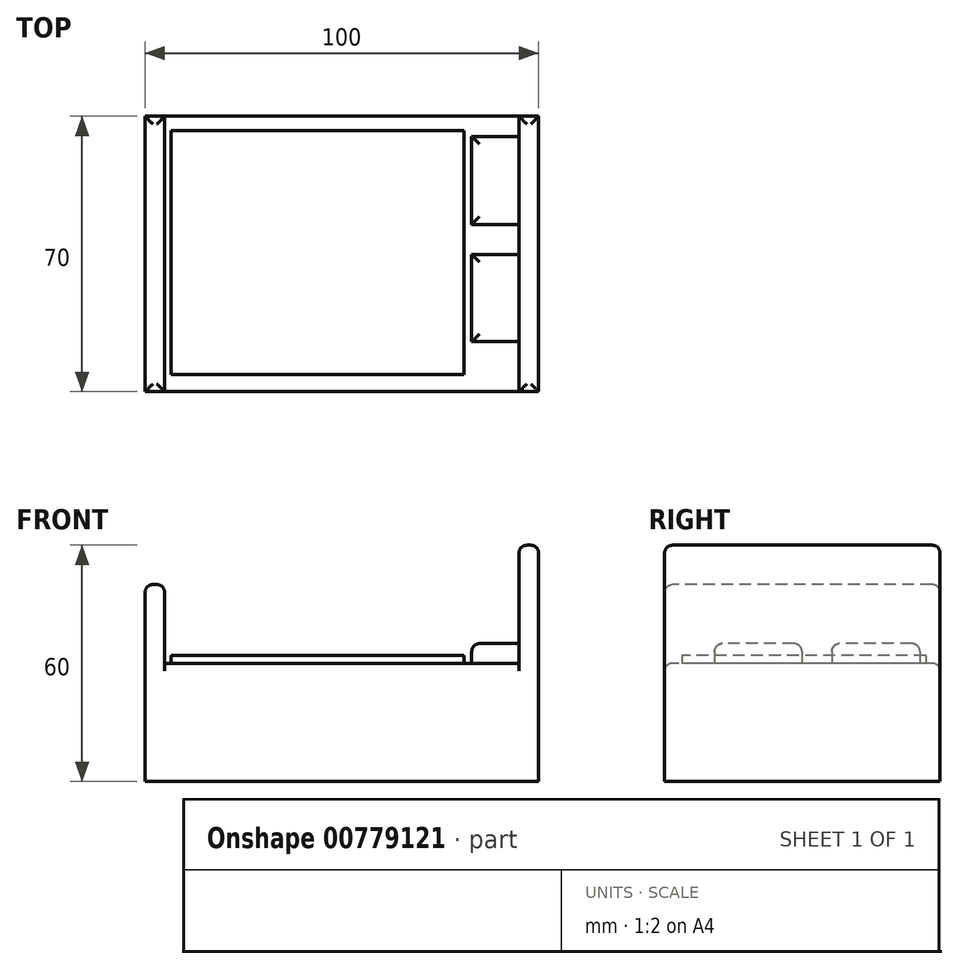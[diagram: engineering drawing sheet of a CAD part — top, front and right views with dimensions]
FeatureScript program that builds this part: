
annotation { "Feature Type Name" : "Feature", "Feature Type Description" : "" }
export const myFeature = defineFeature(function(context is Context, id is Id, definition is map)
    precondition{}
    {
        {
            var Q0;
            Q0=qCreatedBy(makeId("Top.planeOp"),FACE);
            var sketch = newSketch(context, id + "F0", { "sketchPlane" : qUnion([Q0])});
            skLineSegment(sketch, "E0.bottom", {"start": v(0, 0) * mm, "end": v(100, 0) * mm});
            skLineSegment(sketch, "E0.top", {"start": v(0, 70) * mm, "end": v(100, 70) * mm});
            skLineSegment(sketch, "E0.left", {"start": v(0, 0) * mm, "end": v(0, 70) * mm});
            skLineSegment(sketch, "E0.right", {"start": v(100, 0) * mm, "end": v(100, 70) * mm});
            skSolve(sketch);
        }
        {
            var Q0;
            Q0=makeQuery(id+"F0.imprint","IMPRINT",FACE,{"disambiguationData":[TD([[makeQuery(id+"F0.imprint","IMPRINT",EDGE,{"derivedFrom":sQuery(id+"F0.wireOp",EDGE,"E0.bottom")}),1.0]])]});
            extrude(context, id + "F1", {"entities" : qUnion([Q0]), "depth" : 30 * mm, "offsetDistance" : 25 * mm});
        }
        {
            var Q0;
            Q0=makeQuery(id+"F1.opExtrude","CAP_FACE",FACE,{"disambiguationData":[OSD([sQuery(id+"F0.wireOp",EDGE,"E0.bottom"),sQuery(id+"F0.wireOp",EDGE,"E0.top"),sQuery(id+"F0.wireOp",EDGE,"E0.left"),sQuery(id+"F0.wireOp",EDGE,"E0.right")])],"isStart":false});
            var sketch = newSketch(context, id + "F2", { "sketchPlane" : qUnion([Q0])});
            skLineSegment(sketch, "E1.bottom", {"start": v(95, 70) * mm, "end": v(100, 70) * mm});
            skLineSegment(sketch, "E1.top", {"start": v(95, 0) * mm, "end": v(100, 0) * mm});
            skLineSegment(sketch, "E1.left", {"start": v(95, 70) * mm, "end": v(95, 0) * mm});
            skLineSegment(sketch, "E1.right", {"start": v(100, 70) * mm, "end": v(100, 0) * mm});
            skSolve(sketch);
        }
        {
            var Q0;
            Q0 = qSketchRegion(id + "F2", true);
            extrude(context, id + "F3", {"entities" : qUnion([Q0]), "operationType" : NewBodyOperationType.ADD, "depth" : 30 * mm, "offsetDistance" : 25 * mm});
        }
        {
            var Q0;
            Q0=makeQuery(id+"F1.opExtrude","CAP_FACE",FACE,{"disambiguationData":[OSD([sQuery(id+"F0.wireOp",EDGE,"E0.bottom"),sQuery(id+"F0.wireOp",EDGE,"E0.top"),sQuery(id+"F0.wireOp",EDGE,"E0.left"),sQuery(id+"F0.wireOp",EDGE,"E0.right")])],"isStart":false});
            var sketch = newSketch(context, id + "F4", { "sketchPlane" : qUnion([Q0])});
            skLineSegment(sketch, "E2.bottom", {"start": v(83, 64.86) * mm, "end": v(95, 64.86) * mm});
            skLineSegment(sketch, "E2.top", {"start": v(83, 42.47) * mm, "end": v(95, 42.47) * mm});
            skLineSegment(sketch, "E2.left", {"start": v(83, 64.86) * mm, "end": v(83, 42.47) * mm});
            skLineSegment(sketch, "E2.right", {"start": v(95, 64.86) * mm, "end": v(95, 42.47) * mm});
            skLineSegment(sketch, "E3.bottom", {"start": v(83, 34.88) * mm, "end": v(95, 34.88) * mm});
            skLineSegment(sketch, "E3.top", {"start": v(83, 12.7) * mm, "end": v(95, 12.7) * mm});
            skLineSegment(sketch, "E3.left", {"start": v(83, 34.88) * mm, "end": v(83, 12.7) * mm});
            skLineSegment(sketch, "E3.right", {"start": v(95, 34.88) * mm, "end": v(95, 12.7) * mm});
            skSolve(sketch);
        }
        {
            var Q0;
            Q0=makeQuery(id+"F4.imprint","IMPRINT",FACE,{"disambiguationData":[TD([[makeQuery(id+"F4.imprint","IMPRINT",EDGE,{"derivedFrom":sQuery(id+"F4.wireOp",EDGE,"E3.bottom")}),-1.0]])]});
            var Q1;
            Q1=makeQuery(id+"F4.imprint","IMPRINT",FACE,{"disambiguationData":[TD([[makeQuery(id+"F4.imprint","IMPRINT",EDGE,{"derivedFrom":sQuery(id+"F4.wireOp",EDGE,"E2.bottom")}),-1.0]])]});
            extrude(context, id + "F5", {"entities" : qUnion([Q0, Q1]), "operationType" : NewBodyOperationType.ADD, "depth" : 5 * mm, "offsetDistance" : 25 * mm});
        }
        {
            var Q0;
            Q0=makeQuery(id+"F1.opExtrude","CAP_FACE",FACE,{"disambiguationData":[OSD([sQuery(id+"F0.wireOp",EDGE,"E0.bottom"),sQuery(id+"F0.wireOp",EDGE,"E0.top"),sQuery(id+"F0.wireOp",EDGE,"E0.left"),sQuery(id+"F0.wireOp",EDGE,"E0.right")])],"isStart":false});
            var sketch = newSketch(context, id + "F6", { "sketchPlane" : qUnion([Q0])});
            skLineSegment(sketch, "E4.bottom", {"start": v(0, 70) * mm, "end": v(5, 70) * mm});
            skLineSegment(sketch, "E4.top", {"start": v(0, 0) * mm, "end": v(5, 0) * mm});
            skLineSegment(sketch, "E4.left", {"start": v(0, 70) * mm, "end": v(0, 0) * mm});
            skLineSegment(sketch, "E4.right", {"start": v(5, 70) * mm, "end": v(5, 0) * mm});
            skSolve(sketch);
        }
        {
            var Q0;
            Q0 = qSketchRegion(id + "F6", true);
            extrude(context, id + "F7", {"entities" : qUnion([Q0]), "operationType" : NewBodyOperationType.ADD, "depth" : 20 * mm, "offsetDistance" : 25 * mm});
        }
        {
            var Q0;
            Q0=makeQuery(id+"F5.opExtrude","CAP_EDGE",EDGE,{"disambiguationData":[OSD([sQuery(id+"F4.wireOp",EDGE,"E3.left")])],"isStart":false});
            var Q1;
            Q1=makeQuery(id+"F5.opExtrude","CAP_EDGE",EDGE,{"disambiguationData":[OSD([sQuery(id+"F4.wireOp",EDGE,"E3.top")])],"isStart":false});
            var Q2;
            Q2=makeQuery(id+"F5.opExtrude","CAP_EDGE",EDGE,{"disambiguationData":[OSD([sQuery(id+"F4.wireOp",EDGE,"E3.bottom")])],"isStart":false});
            var Q3;
            Q3=makeQuery(id+"F5.opExtrude","CAP_EDGE",EDGE,{"disambiguationData":[OSD([sQuery(id+"F4.wireOp",EDGE,"E2.left")])],"isStart":false});
            var Q4;
            Q4=makeQuery(id+"F5.opExtrude","CAP_EDGE",EDGE,{"disambiguationData":[OSD([sQuery(id+"F4.wireOp",EDGE,"E2.top")])],"isStart":false});
            var Q5;
            Q5=makeQuery(id+"F5.opExtrude","CAP_EDGE",EDGE,{"disambiguationData":[OSD([sQuery(id+"F4.wireOp",EDGE,"E2.bottom")])],"isStart":false});
            var Q6;
            Q6=makeQuery(id+"F1.opExtrude","CAP_EDGE",EDGE,{"disambiguationData":[OSD([sQuery(id+"F0.wireOp",EDGE,"E0.bottom")])],"isStart":false});
            var Q7;
            Q7=makeQuery(id+"F1.opExtrude","CAP_EDGE",EDGE,{"disambiguationData":[OSD([sQuery(id+"F0.wireOp",EDGE,"E0.top")])],"isStart":false});
            var Q8;
            Q8=makeQuery(id+"F7.opExtrude","CAP_EDGE",EDGE,{"disambiguationData":[OSD([sQuery(id+"F6.wireOp",EDGE,"E4.top")])],"isStart":false});
            var Q9;
            Q9=makeQuery(id+"F7.opExtrude","CAP_EDGE",EDGE,{"disambiguationData":[OSD([sQuery(id+"F6.wireOp",EDGE,"E4.bottom")])],"isStart":false});
            var Q10;
            Q10=makeQuery(id+"F3.opExtrude","CAP_EDGE",EDGE,{"disambiguationData":[OSD([sQuery(id+"F2.wireOp",EDGE,"E1.top")])],"isStart":false});
            var Q11;
            Q11=makeQuery(id+"F3.opExtrude","CAP_EDGE",EDGE,{"disambiguationData":[OSD([sQuery(id+"F2.wireOp",EDGE,"E1.bottom")])],"isStart":false});
            var Q12;
            Q12=makeQuery(id+"F3.opExtrude","CAP_EDGE",EDGE,{"disambiguationData":[OSD([sQuery(id+"F2.wireOp",EDGE,"E1.left")])],"isStart":false});
            var Q13;
            Q13=makeQuery(id+"F3.opExtrude","CAP_EDGE",EDGE,{"disambiguationData":[OSD([sQuery(id+"F2.wireOp",EDGE,"E1.right")])],"isStart":false});
            var Q14;
            Q14=makeQuery(id+"F7.opExtrude","CAP_EDGE",EDGE,{"disambiguationData":[OSD([sQuery(id+"F6.wireOp",EDGE,"E4.right")])],"isStart":false});
            var Q15;
            Q15=makeQuery(id+"F7.opExtrude","CAP_EDGE",EDGE,{"disambiguationData":[OSD([sQuery(id+"F6.wireOp",EDGE,"E4.left")])],"isStart":false});
            fillet(context, id + "F8", {"entities" : qUnion([Q0, Q1, Q2, Q3, Q4, Q5, Q6, Q7, Q8, Q9, Q10, Q11, Q12, Q13, Q14, Q15]), "radius" : 2 * mm, "tangentPropagation" : true, "allowEdgeOverflow" : false});
        }
        {
            var Q0;
            Q0=makeQuery(id+"F1.opExtrude","CAP_FACE",FACE,{"disambiguationData":[OSD([sQuery(id+"F0.wireOp",EDGE,"E0.bottom"),sQuery(id+"F0.wireOp",EDGE,"E0.top"),sQuery(id+"F0.wireOp",EDGE,"E0.left"),sQuery(id+"F0.wireOp",EDGE,"E0.right")])],"isStart":false});
            var sketch = newSketch(context, id + "F9", { "sketchPlane" : qUnion([Q0])});
            skLineSegment(sketch, "E5.bottom", {"start": v(6.62, 66.34) * mm, "end": v(80.98, 66.34) * mm});
            skLineSegment(sketch, "E5.top", {"start": v(6.62, 4.38) * mm, "end": v(80.98, 4.38) * mm});
            skLineSegment(sketch, "E5.left", {"start": v(6.62, 66.34) * mm, "end": v(6.62, 4.38) * mm});
            skLineSegment(sketch, "E5.right", {"start": v(80.98, 66.34) * mm, "end": v(80.98, 4.38) * mm});
            skSolve(sketch);
        }
        {
            var Q0;
            Q0=makeQuery(id+"F9.imprint","IMPRINT",FACE,{"disambiguationData":[TD([[makeQuery(id+"F9.imprint","IMPRINT",EDGE,{"derivedFrom":sQuery(id+"F9.wireOp",EDGE,"E5.bottom")}),-1.0]])]});
            extrude(context, id + "F10", {"entities" : qUnion([Q0]), "operationType" : NewBodyOperationType.ADD, "depth" : 2 * mm, "offsetDistance" : 25 * mm});
        }
    });
